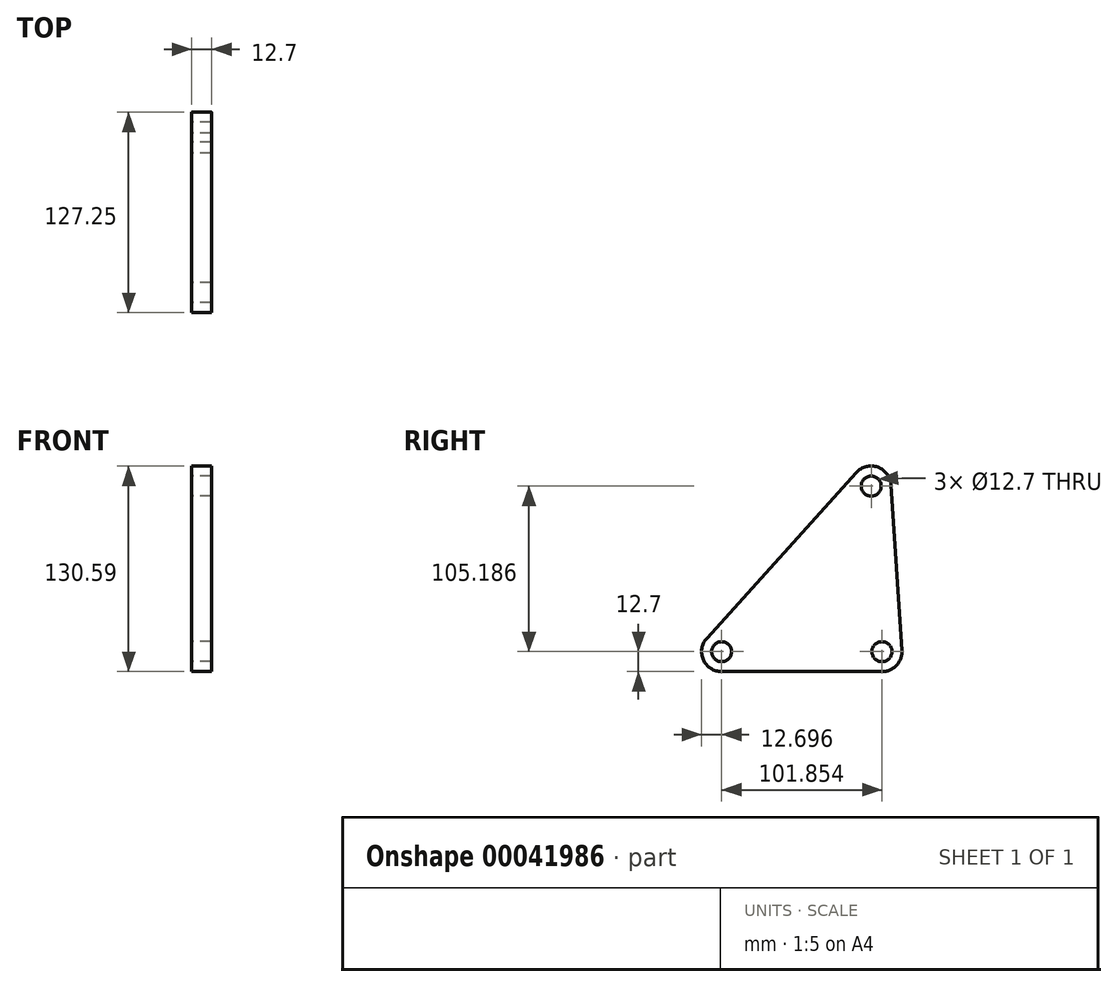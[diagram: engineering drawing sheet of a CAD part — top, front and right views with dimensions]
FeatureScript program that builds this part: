
annotation { "Feature Type Name" : "Feature", "Feature Type Description" : "" }
export const myFeature = defineFeature(function(context is Context, id is Id, definition is map)
    precondition{}
    {
        {
            var Q0;
            Q0=qCreatedBy(makeId("Right.planeOp"),FACE);
            var sketch = newSketch(context, id + "F0", { "sketchPlane" : qUnion([Q0])});
            skLineSegment(sketch, "E0", {"start": v(0, 0) * mm, "end": v(-6.86, 105.19) * mm, "construction": true});
            skLineSegment(sketch, "E1", {"start": v(-6.86, 105.19) * mm, "end": v(-101.85, 0) * mm, "construction": true});
            skLineSegment(sketch, "E2", {"start": v(-101.85, 0) * mm, "end": v(0, 0) * mm, "construction": true});
            skLineSegment(sketch, "E3.0", {"start": v(-16.29, 113.7) * mm, "end": v(-111.28, 8.51) * mm});
            skLineSegment(sketch, "E3.1", {"start": v(12.67, 0.83) * mm, "end": v(5.81, 106.01) * mm});
            skLineSegment(sketch, "E3.2", {"start": v(-101.85, -12.7) * mm, "end": v(0, -12.7) * mm});
            skPoint(sketch, "E4.visualSharp", {"position": v(-130.44, -12.7) * mm});
            skArc(sketch, "E4.filletArc", {"start": v(-111.28, 8.51) * mm, "mid": v(-113.46, -5.16) * mm, "end": v(-101.85, -12.7) * mm});
            skPoint(sketch, "E5.visualSharp", {"position": v(3.86, 136) * mm});
            skArc(sketch, "E5.filletArc", {"start": v(5.81, 106.01) * mm, "mid": v(-2.69, 117.18) * mm, "end": v(-16.29, 113.7) * mm});
            skPoint(sketch, "E6.visualSharp", {"position": v(13.56, -12.7) * mm});
            skArc(sketch, "E6.filletArc", {"start": v(0, -12.7) * mm, "mid": v(9.27, -8.68) * mm, "end": v(12.67, 0.83) * mm});
            skCircle(sketch, "E7", {"center": v(-6.86, 105.19) * mm, "radius": 6.35 * mm});
            skCircle(sketch, "E8", {"center": v(0, 0) * mm, "radius": 6.35 * mm});
            skCircle(sketch, "E9", {"center": v(-101.85, 0) * mm, "radius": 6.35 * mm});
            skSolve(sketch);
        }
        {
            var Q0;
            Q0=makeQuery(id+"F0.imprint","IMPRINT",FACE,{"disambiguationData":[TD([[makeQuery(id+"F0.imprint","IMPRINT",EDGE,{"derivedFrom":sQuery(id+"F0.wireOp",EDGE,"E3.0")}),1.0]])]});
            extrude(context, id + "F1", {"entities" : qUnion([Q0]), "depth" : 12.7 * mm});
        }
    });
